FCSTD DOCUMENT  (FreeCAD 0.21R33771 (Git))
Label: Noise_Toaster_Classic
License: All rights reserved
LicenseURL: http://en.wikipedia.org/wiki/All_rights_reserved
objects: App::Link×10, App::DocumentObjectGroup×3, PartDesign::CoordinateSystem×1, App::FeaturePython×1, App::Part×1, Spreadsheet::Sheet×1, Image::ImagePlane×1
note: 1 computed .brp shape members not serialized (recipe doc carries the construction recipe); baked Part::Feature solids carry a one-line shape summary decoded from their .brp
EXTERNAL_REF file=Front_Panel.FCStd obj=Body
EXTERNAL_REF file=Side_Panel-B.FCStd obj=SP_B_LCS
EXTERNAL_REF file=Side_Panel-B.FCStd obj=Body
EXTERNAL_REF file=Side_Panel-A.FCStd obj=Body
EXTERNAL_REF file=Back_Panel.FCStd obj=Body

FEATURE [PartDesign::CoordinateSystem] LCS_Origin
  AttacherType = Attacher::AttachEngine3D
  MapMode = 2
  Support = -> [X_Axis]
FEATURE [App::DocumentObjectGroup] Constraints
FEATURE [App::FeaturePython] Variables  # WARN: FeaturePython — macro-defined, semantics opaque (R4)
  Type = App::PropertyContainer
FEATURE [App::DocumentObjectGroup] Configurations
FEATURE [App::Link] Link  label="Link - Back_Panel"
FEATURE [App::Link] Link001  label="Link - Front_Panel"
FEATURE [App::Link] Link002  label="Link - Side_Panel-A"
FEATURE [App::Link] Link003  label="Link - Side_Panle-B"
FEATURE [App::DocumentObjectGroup] Parts
  Group = -> [Link,Link001,Link002,Link003]
FEATURE [App::Link] Front001  label="Frontpanel"
  LinkPlacement = pos=(0,0,77.5) rot=(0,0,1;0rad)
  LinkedObject = -> <external Front_Panel.FCStd>#Body
  Placement = pos=(0,0,77.5) rot=(0,0,1;0rad)
  expr: .Placement.Base.z = <<measurements>>.Side_A_height - Front_Panel#<<measurements>>.Front_thickness
FEATURE [App::Link] Top
  AttachedBy = #SP_B_LCS
  AttachedTo = Parent Assembly#LCS_Origin
  LinkedObject = -> <external Side_Panel-B.FCStd>#Body
  SolverId = Asm4EE
  expr: Placement = LCS_Origin.Placement * AttachmentOffset * Side_Panel_B#SP_B_LCS.Placement ^ -1
FEATURE [App::Link] Left
  AttachedBy = #SP_A_LCS
  AttachedTo = Parent Assembly#LCS_Origin
  LinkPlacement = pos=(-3,0,0) rot=(0,0,1;0rad)
  LinkedObject = -> <external Side_Panel-A.FCStd>#Body
  Placement = pos=(-3,0,0) rot=(0,0,1;0rad)
  SolverId = Asm4EE
  expr: .Placement.Base.x = -Front_Panel#<<measurements>>.Side_B_o_thickness
FEATURE [App::Link] Right
  AttachedBy = #SP_A_LCS
  AttachedTo = Parent Assembly#LCS_Origin
  LinkPlacement = pos=(-3,175.1,0) rot=(0,0,1;0rad)
  LinkedObject = -> <external Side_Panel-A.FCStd>#Body
  Placement = pos=(-3,175.1,0) rot=(0,0,1;0rad)
  SolverId = Asm4EE
  expr: .Placement.Base.x = -Front_Panel#<<measurements>>.Side_B_o_thickness
  expr: .Placement.Base.y = Front_Panel#<<measurements>>.Front_width + Front_Panel#<<measurements>>.Side_A_thickness
FEATURE [App::Link] Back
  AttachedBy = #BP_LCS
  AttachedTo = Parent Assembly#LCS_Origin
  LinkPlacement = pos=(-3,-10,0) rot=(0,0,1;0rad)
  LinkedObject = -> <external Back_Panel.FCStd>#Body
  Placement = pos=(-3,-10,0) rot=(0,0,1;0rad)
  SolverId = Asm4EE
  expr: .Placement.Base.x = -Front_Panel#<<measurements>>.Side_B_o_thickness
  expr: .Placement.Base.y = -Front_Panel#<<measurements>>.Side_A_thickness
FEATURE [App::Link] Bottom
  AttachedBy = #SP_B_LCS
  AttachedTo = Parent Assembly#LCS_Origin
  AttachmentOffset = pos=(0,0,0) rot=(0,0,1;3.14159rad)
  LinkPlacement = pos=(165.1,165.1,0) rot=(0,0,1;3.14159rad)
  LinkedObject = -> <external Side_Panel-B.FCStd>#Body
  Placement = pos=(165.1,165.1,0) rot=(0,0,1;3.14159rad)
  SolverId = Asm4EE
  expr: .Placement.Base.x = Front_Panel#<<measurements>>.Front_height
  expr: .Placement.Base.y = Front_Panel#<<measurements>>.Front_width
FEATURE [App::Part] Assembly
  AssemblyType = Part::Link
  Group = -> [LCS_Origin,Constraints,Variables,Configurations,Front001,Top,Left,Right,Back,Bottom]
  Origin = -> Origin
  Type = Assembly
FEATURE [Spreadsheet::Sheet] Spreadsheet  label="measurements"
  cells = B2='Front Panel; B3='material; D3(Front_material)='Alu, Melal; B4='material thickness*; D4(Front_thickness)==2.5 mm; B5='measurements; B6='width*; D6(Front_width)==165.1 mm; B7='height; D7(Front_height)==Front_width; B9='Side Panel A; B10='material; D10(Side_A_material)='Wood, MDF; B11='material thickness*; D11(Side_A_thickness)==10 mm; B12='measurements; B13='width; D13(Side_A_width)==Front_height + 2 * Side_B_o_thickness; B14='height*; D14(Side_A_height)==80 mm; B16='Side Panlel B; B17='inner; B18='material; D18(Side_B_i_material)='Wood, MDF; B19='material thickness*; D19(Side_B_i_thickness)==10 mm; B20='measurements; B21='width; D21(Side_B_i_width)==Front_width; B22='height; D22(Side_B_i_height)==Side_B_o_height - Side_B_o_thickness; B23='outer; B24='material; D24(Side_B_o_material)='Wood, MDF; B25='material thickness*; D25(Side_B_o_thickness)==3 mm; B26='measurements; B27='width; D27(Side_B_o_width)==Front_width; B28='height; D28(Side_B_o_height)==Side_A_height; B30='Back Panel; B31='material; D31(Back_material)='Wood, MDF; B32='material thickness*; D32(Back_thickness)==3 mm; B33='measurements; B34='width; D34(Back_width)==Front_width + 2 * Side_A_thickness; B35='height; D35(Back_height)==Side_A_width; B37='* = reference measure
FEATURE [Image::ImagePlane] front_panel_classic_design  label="front panel classic design"
  Placement = pos=(82.55,82.55,80) rot=(0,0,1;1.5708rad)
  XSize = 257.211
  YSize = 194.496
  expr: .Placement.Base.x = <<measurements>>.Front_width / 2
  expr: .Placement.Base.y = <<measurements>>.Front_height / 2
  expr: .Placement.Base.z = <<measurements>>.Side_A_height

RESOLVED EXTERNAL PARTS (link-assembly join: the EXTERNAL_REF files above that resolve inside this repo's crawl, each included once):
---- part Back_Panel.FCStd = doc fcstd_5dd3100f07a6 ----
FCSTD DOCUMENT  (FreeCAD 0.21R33771 (Git))
Label: Back_Panel
License: All rights reserved
LicenseURL: http://en.wikipedia.org/wiki/All_rights_reserved
objects: Sketcher::SketchObject×1, PartDesign::Pad×1, PartDesign::CoordinateSystem×1, PartDesign::Body×1
note: 5 computed .brp shape members not serialized (recipe doc carries the construction recipe); baked Part::Feature solids carry a one-line shape summary decoded from their .brp
EXTERNAL_REF file=Noise_Toaster_Classic.FCStd obj=Spreadsheet

FEATURE [Sketcher::SketchObject] Sketch
  FullyConstrained = true
  MapMode = 5
  Support = -> [XY_Plane]
  expr: Constraints[10] = Noise_Toaster_Classic#<<measurements>>.Back_width
  expr: Constraints[9] = Noise_Toaster_Classic#<<measurements>>.Back_height
  sketch-geometry (61):
    g0: LineSegment StartX=0 StartY=0 StartZ=0 EndX=171.1 EndY=0 EndZ=0
    g1: LineSegment StartX=171.1 StartY=0 StartZ=0 EndX=171.1 EndY=185.1 EndZ=0
    g2: LineSegment StartX=171.1 StartY=185.1 StartZ=0 EndX=0 EndY=185.1 EndZ=0
    g3: LineSegment StartX=0 StartY=185.1 StartZ=0 EndX=0 EndY=0 EndZ=0
    g4: Circle CenterX=48.5 CenterY=48.5 CenterZ=0 NormalX=0 NormalY=0 NormalZ=1 AngleXU=0 Radius=2.5
    g5: Circle CenterX=48.5 CenterY=54.5 CenterZ=0 NormalX=0 NormalY=0 NormalZ=1 AngleXU=0 Radius=2.5
    g6: Circle CenterX=48.5 CenterY=60.5 CenterZ=0 NormalX=0 NormalY=0 NormalZ=1 AngleXU=0 Radius=2.5
    g7: Circle CenterX=48.5 CenterY=66.5 CenterZ=0 NormalX=0 NormalY=0 NormalZ=1 AngleXU=0 Radius=2.5
    g8: Circle CenterX=48.5 CenterY=72.5 CenterZ=0 NormalX=0 NormalY=0 NormalZ=1 AngleXU=0 Radius=2.5
    g9: Circle CenterX=48.5 CenterY=42.5 CenterZ=0 NormalX=0 NormalY=0 NormalZ=1 AngleXU=0 Radius=2.5
    g10: Circle CenterX=48.5 CenterY=36.5 CenterZ=0 NormalX=0 NormalY=0 NormalZ=1 AngleXU=0 Radius=2.5
    g11: Circle CenterX=48.5 CenterY=30.5 CenterZ=0 NormalX=0 NormalY=0 NormalZ=1 AngleXU=0 Radius=2.5
    g12: Circle CenterX=48.5 CenterY=24.5 CenterZ=0 NormalX=0 NormalY=0 NormalZ=1 AngleXU=0 Radius=2.5
    g13: Circle CenterX=36.5 CenterY=48.5 CenterZ=0 NormalX=0 NormalY=0 NormalZ=1 AngleXU=0 Radius=2.5
    g14: Circle CenterX=36.5 CenterY=54.5 CenterZ=0 NormalX=0 NormalY=0 NormalZ=1 AngleXU=0 Radius=2.5
    g15: Circle CenterX=36.5 CenterY=60.5 CenterZ=0 NormalX=0 NormalY=0 NormalZ=1 AngleXU=0 Radius=2.5
    g16: Circle CenterX=36.5 CenterY=66.5 CenterZ=0 NormalX=0 NormalY=0 NormalZ=1 AngleXU=0 Radius=2.5
    g17: Circle CenterX=36.5 CenterY=42.5 CenterZ=0 NormalX=0 NormalY=0 NormalZ=1 AngleXU=0 Radius=2.5
    g18: Circle CenterX=36.5 CenterY=36.5 CenterZ=0 NormalX=0 NormalY=0 NormalZ=1 AngleXU=0 Radius=2.5
    g19: Circle CenterX=36.5 CenterY=30.5 CenterZ=0 NormalX=0 NormalY=0 NormalZ=1 AngleXU=0 Radius=2.5
    g20: Circle CenterX=24.5 CenterY=48.5 CenterZ=0 NormalX=0 NormalY=0 NormalZ=1 AngleXU=0 Radius=2.5
    g21: Circle CenterX=24.5 CenterY=54.5 CenterZ=0 NormalX=0 NormalY=0 NormalZ=1 AngleXU=0 Radius=2.5
    g22: Circle CenterX=24.5 CenterY=42.5 CenterZ=0 NormalX=0 NormalY=0 NormalZ=1 AngleXU=0 Radius=2.5
    g23: Circle CenterX=42.5 CenterY=51.5 CenterZ=0 NormalX=0 NormalY=0 NormalZ=1 AngleXU=0 Radius=2.5
    g24: Circle CenterX=42.5 CenterY=45.5 CenterZ=0 NormalX=0 NormalY=0 NormalZ=1 AngleXU=0 Radius=2.5
    g25: Circle CenterX=42.5 CenterY=39.5 CenterZ=0 NormalX=0 NormalY=0 NormalZ=1 AngleXU=0 Radius=2.5
    g26: Circle CenterX=42.5 CenterY=33.5 CenterZ=0 NormalX=0 NormalY=0 NormalZ=1 AngleXU=0 Radius=2.5
    g27: Circle CenterX=42.5 CenterY=27.5 CenterZ=0 NormalX=0 NormalY=0 NormalZ=1 AngleXU=0 Radius=2.5
    g28: Circle CenterX=42.5 CenterY=57.5 CenterZ=0 NormalX=0 NormalY=0 NormalZ=1 AngleXU=0 Radius=2.5
    g29: Circle CenterX=42.5 CenterY=63.5 CenterZ=0 NormalX=0 NormalY=0 NormalZ=1 AngleXU=0 Radius=2.5
    g30: Circle CenterX=42.5 CenterY=69.5 CenterZ=0 NormalX=0 NormalY=0 NormalZ=1 AngleXU=0 Radius=2.5
    g31: Circle CenterX=30.5 CenterY=51.5 CenterZ=0 NormalX=0 NormalY=0 NormalZ=1 AngleXU=0 Radius=2.5
    g32: Circle CenterX=30.5 CenterY=57.5 CenterZ=0 NormalX=0 NormalY=0 NormalZ=1 AngleXU=0 Radius=2.5
    g33: Circle CenterX=30.5 CenterY=63.5 CenterZ=0 NormalX=0 NormalY=0 NormalZ=1 AngleXU=0 Radius=2.5
    g34: Circle CenterX=30.5 CenterY=45.5 CenterZ=0 NormalX=0 NormalY=0 NormalZ=1 AngleXU=0 Radius=2.5
    g35: Circle CenterX=30.5 CenterY=39.5 CenterZ=0 NormalX=0 NormalY=0 NormalZ=1 AngleXU=0 Radius=2.5
    g36: Circle CenterX=30.5 CenterY=33.5 CenterZ=0 NormalX=0 NormalY=0 NormalZ=1 AngleXU=0 Radius=2.5
    g37: Circle CenterX=54.5 CenterY=69.5 CenterZ=0 NormalX=0 NormalY=0 NormalZ=1 AngleXU=0 Radius=2.5
    g38: Circle CenterX=54.5 CenterY=63.5 CenterZ=0 NormalX=0 NormalY=0 NormalZ=1 AngleXU=0 Radius=2.5
    g39: Circle CenterX=54.5 CenterY=57.5 CenterZ=0 NormalX=0 NormalY=0 NormalZ=1 AngleXU=0 Radius=2.5
    g40: Circle CenterX=54.5 CenterY=51.5 CenterZ=0 NormalX=0 NormalY=0 NormalZ=1 AngleXU=0 Radius=2.5
    g41: Circle CenterX=54.5 CenterY=45.5 CenterZ=0 NormalX=0 NormalY=0 NormalZ=1 AngleXU=0 Radius=2.5
    g42: Circle CenterX=54.5 CenterY=39.5 CenterZ=0 NormalX=0 NormalY=0 NormalZ=1 AngleXU=0 Radius=2.5
    g43: Circle CenterX=54.5 CenterY=33.5 CenterZ=0 NormalX=0 NormalY=0 NormalZ=1 AngleXU=0 Radius=2.5
    g44: Circle CenterX=54.5 CenterY=27.5 CenterZ=0 NormalX=0 NormalY=0 NormalZ=1 AngleXU=0 Radius=2.5
    g45: Circle CenterX=60.5 CenterY=66.5 CenterZ=0 NormalX=0 NormalY=0 NormalZ=1 AngleXU=0 Radius=2.5
    g46: Circle CenterX=60.5 CenterY=60.5 CenterZ=0 NormalX=0 NormalY=0 NormalZ=1 AngleXU=0 Radius=2.5
    g47: Circle CenterX=60.5 CenterY=54.5 CenterZ=0 NormalX=0 NormalY=0 NormalZ=1 AngleXU=0 Radius=2.5
    g48: Circle CenterX=60.5 CenterY=48.5 CenterZ=0 NormalX=0 NormalY=0 NormalZ=1 AngleXU=0 Radius=2.5
    g49: Circle CenterX=60.5 CenterY=42.5 CenterZ=0 NormalX=0 NormalY=0 NormalZ=1 AngleXU=0 Radius=2.5
    g50: Circle CenterX=60.5 CenterY=36.5 CenterZ=0 NormalX=0 NormalY=0 NormalZ=1 AngleXU=0 Radius=2.5
    g51: Circle CenterX=60.5 CenterY=30.5 CenterZ=0 NormalX=0 NormalY=0 NormalZ=1 AngleXU=0 Radius=2.5
    g52: Circle CenterX=66.5 CenterY=63.5 CenterZ=0 NormalX=0 NormalY=0 NormalZ=1 AngleXU=0 Radius=2.5
    g53: Circle CenterX=66.5 CenterY=57.5 CenterZ=0 NormalX=0 NormalY=0 NormalZ=1 AngleXU=0 Radius=2.5
    g54: Circle CenterX=66.5 CenterY=51.5 CenterZ=0 NormalX=0 NormalY=0 NormalZ=1 AngleXU=0 Radius=2.5
    g55: Circle CenterX=66.5 CenterY=45.5 CenterZ=0 NormalX=0 NormalY=0 NormalZ=1 AngleXU=0 Radius=2.5
    g56: Circle CenterX=66.5 CenterY=39.5 CenterZ=0 NormalX=0 NormalY=0 NormalZ=1 AngleXU=0 Radius=2.5
    g57: Circle CenterX=66.5 CenterY=33.5 CenterZ=0 NormalX=0 NormalY=0 NormalZ=1 AngleXU=0 Radius=2.5
    g58: Circle CenterX=72.5 CenterY=54.5 CenterZ=0 NormalX=0 NormalY=0 NormalZ=1 AngleXU=0 Radius=2.5
    g59: Circle CenterX=72.5 CenterY=48.5 CenterZ=0 NormalX=0 NormalY=0 NormalZ=1 AngleXU=0 Radius=2.5
    g60: Circle CenterX=72.5 CenterY=42.5 CenterZ=0 NormalX=0 NormalY=0 NormalZ=1 AngleXU=0 Radius=2.5
  constraints (182):
    c: Coincident(g0,g1)
    c: Coincident(g1,g2)
    c: Coincident(g2,g3)
    c: Coincident(g3,g0)
    c: Horizontal(g0)
    c: Horizontal(g2)
    c: Vertical(g1)
    c: Vertical(g3)
    c: Coincident(g0,g-1)
    c: DistanceX(g2,g2) = 171.1
    c: DistanceY(g3,g3) = 185.1
    c: Radius(g4) = 2.5
    c: Vertical(g7,g6)
    c: Vertical(g6,g5)
    c: Equal(g4,g5)
    c: Equal(g5,g6)
    c: Equal(g6,g7)
    c: Vertical(g8,g7)
    c: Equal(g8,g7)
    c: Distance(g6,g5) = 6
    c: Distance(g7,g6) = 6
    c: Distance(g8,g7) = 6
    c: Equal(g9,g10)
    c: Equal(g10,g11)
    c: Equal(g11,g12)
    c: Equal(g4,g9)
    c: Vertical(g9,g10)
    c: Vertical(g10,g11)
    c: Vertical(g11,g12)
    c: Distance(g9,g10) = 6
    c: Distance(g10,g11) = 6
    c: Distance(g11,g12) = 6
    c: Vertical(g13,g14)
    c: Vertical(g14,g15)
    c: Vertical(g15,g16)
    c: Radius(g13) = 2.5
    c: Equal(g13,g14)
    c: Equal(g14,g15)
    c: Equal(g15,g16)
    c: Equal(g13,g17)
    c: Equal(g17,g18)
    c: Equal(g18,g19)
    c: Vertical(g13,g17)
    c: Vertical(g17,g18)
    c: Vertical(g18,g19)
    c: Distance(g16,g15) = 6
    c: Distance(g15,g14) = 6
    c: Distance(g13,g14) = 6
    c: Distance(g13,g17) = 6
    c: Distance(g18,g17) = 6
    c: Distance(g19,g18) = 6
    c: Vertical(g22,g20)
    c: Vertical(g20,g21)
    c: Distance(g13,g20) = 12
    c: Radius(g20) = 2.5
    c: Equal(g20,g21)
    c: Distance(g20,g21) = 6
    c: Distance(g20,g22) = 6
    c: Horizontal(g13,g20)
    c: Equal(g20,g22)
    c: Vertical(g34,g35)
    c: Vertical(g35,g36)
    c: Vertical(g36,g31)
    c: Vertical(g31,g32)
    c: Vertical(g32,g33)
    c: Vertical(g26,g27)
    c: Vertical(g27,g25)
    c: Vertical(g25,g24)
    c: Vertical(g24,g23)
    c: Vertical(g23,g28)
    c: Vertical(g28,g29)
    c: Vertical(g29,g30)
    c: Equal(g4,g24)
    c: Equal(g24,g25)
    c: Equal(g25,g26)
    c: Equal(g26,g27)
    c: Equal(g27,g23)
    c: Equal(g23,g28)
    c: Equal(g28,g29)
    c: Equal(g29,g30)
    c: Equal(g30,g33)
    c: Equal(g33,g32)
    c: Equal(g32,g31)
    c: Equal(g31,g34)
    c: Equal(g34,g35)
    c: Equal(g35,g36)
    c: Distance(g30,g29) = 6
    c: Distance(g29,g28) = 6
    c: Distance(g28,g23) = 6
    c: Distance(g23,g24) = 6
    c: Distance(g24,g25) = 6
    c: Distance(g25,g26) = 6
    c: Distance(g26,g27) = 6
    c: Distance(g36,g35) = 6
    c: Distance(g34,g35) = 6
    c: Distance(g31,g34) = 6
    c: Distance(g32,g31) = 6
    c: Distance(g33,g32) = 6
    c: Distance(g23,g31) = 12
    c: Horizontal(g23,g31)
    c: Equal(g11,g43)
    c: Equal(g43,g42)
    c: Equal(g42,g41)
    c: Equal(g41,g40)
    c: Equal(g40,g39)
    c: Equal(g39,g38)
    c: Equal(g38,g37)
    c: Equal(g37,g44)
    c: Vertical(g37,g38)
    c: Vertical(g38,g39)
    c: Vertical(g39,g40)
    c: Vertical(g40,g41)
    c: Vertical(g41,g42)
    c: Vertical(g42,g43)
    c: Vertical(g43,g44)
    c: Horizontal(g37,g30)
    c: DistanceX(g30,g37) = 12
    c: Distance(g37,g38) = 6
    c: Distance(g38,g39) = 6
    c: Distance(g39,g40) = 6
    c: Distance(g40,g41) = 6
    c: Distance(g41,g42) = 6
    c: Distance(g42,g43) = 6
    c: Distance(g43,g44) = 6
    c: Vertical(g45,g46)
    c: Vertical(g46,g47)
    c: Vertical(g47,g48)
    c: Vertical(g48,g49)
    c: Vertical(g49,g50)
    c: Vertical(g50,g51)
    c: Equal(g45,g46)
    c: Equal(g46,g47)
    c: Equal(g47,g48)
    c: Equal(g48,g49)
    c: Equal(g49,g50)
    c: Equal(g50,g51)
    c: Equal(g51,g37)
    c: Horizontal(g45,g7)
    c: Distance(g45,g46) = 6
    c: Distance(g46,g47) = 6
    c: Distance(g47,g48) = 6
    c: Distance(g48,g49) = 6
    c: Distance(g49,g50) = 6
    c: Distance(g50,g51) = 6
    c: Vertical(g52,g53)
    c: Vertical(g53,g54)
    c: Vertical(g54,g55)
    c: Vertical(g55,g56)
    c: Vertical(g56,g57)
    c: Equal(g52,g53)
    c: Equal(g53,g54)
    c: Equal(g54,g55)
    c: Equal(g55,g56)
    c: Equal(g56,g57)
    c: Equal(g57,g45)
    c: DistanceY(g53,g52) = 6
    c: DistanceY(g54,g53) = 6
    c: DistanceY(g55,g54) = 6
    c: DistanceY(g56,g55) = 6
    c: DistanceX(g43,g57) = 12
    c: Horizontal(g57,g43)
    c: Distance(g57,g56) = 6
    c: Equal(g58,g59)
    c: Equal(g59,g60)
    c: Equal(g60,g53)
    c: Vertical(g58,g59)
    c: Vertical(g59,g60)
    c: Horizontal(g59,g48)
    c: DistanceY(g59,g58) = 6
    c: DistanceY(g60,g59) = 6
    c: DistanceX(g48,g59) = 12
    c: Distance(g4,g0) = 48.5
    c: Distance(g4,g3) = 48.5
    c: DistanceX(g4,g40) = 6
    c: DistanceX(g14,g5) = 12
    c: DistanceY(g24,g4) = 3
    c: Vertical(g9,g4)
    c: DistanceY(g9,g4) = 6
    c: DistanceY(g4,g5) = 6
    c: Vertical(g5,g4)
    c: DistanceX(g5,g47) = 12
    c: Horizontal(g5,g14)
FEATURE [PartDesign::Pad] Pad
  Direction = (0,0,1)
  Length = 3
  Length2 = 10
  Profile = -> Sketch
  ReferenceAxis = -> Sketch [N_Axis]
  Reversed = true
  Type = 0
  expr: Length = Noise_Toaster_Classic#<<measurements>>.Back_thickness
FEATURE [PartDesign::CoordinateSystem] BP_LCS
  AttacherType = Attacher::AttachEngine3D
  Support = -> [Pad]
FEATURE [PartDesign::Body] Body  label="Körper"
  Group = -> [Sketch,Pad,BP_LCS]
  Origin = -> Origin
  Tip = -> Pad
---- part Front_Panel.FCStd = doc fcstd_5506be05636f ----
FCSTD DOCUMENT  (FreeCAD 0.21R33771 (Git))
Label: Front_Panel
License: All rights reserved
LicenseURL: http://en.wikipedia.org/wiki/All_rights_reserved
objects: Sketcher::SketchObject×1, PartDesign::Pad×1, PartDesign::CoordinateSystem×1, PartDesign::Body×1
note: 5 computed .brp shape members not serialized (recipe doc carries the construction recipe); baked Part::Feature solids carry a one-line shape summary decoded from their .brp
EXTERNAL_REF file=Noise_Toaster_Classic.FCStd obj=Spreadsheet

FEATURE [Sketcher::SketchObject] Sketch  label="dimensions"
  FullyConstrained = true
  Support = -> [XY_Plane]
  expr: Constraints[9] = Noise_Toaster_Classic#<<measurements>>.Front_width
  sketch-geometry (33):
    g0: LineSegment StartX=0 StartY=0 StartZ=0 EndX=165.1 EndY=0 EndZ=0
    g1: LineSegment StartX=165.1 StartY=0 StartZ=0 EndX=165.1 EndY=165.1 EndZ=0
    g2: LineSegment StartX=165.1 StartY=165.1 StartZ=0 EndX=0 EndY=165.1 EndZ=0
    g3: LineSegment StartX=0 StartY=165.1 StartZ=0 EndX=0 EndY=0 EndZ=0
    g4: Circle CenterX=5 CenterY=157.6 CenterZ=0 NormalX=0 NormalY=0 NormalZ=1 AngleXU=0 Radius=2
    g5: Circle CenterX=5 CenterY=7.5 CenterZ=0 NormalX=0 NormalY=0 NormalZ=1 AngleXU=0 Radius=2
    g6: Circle CenterX=160.1 CenterY=7.5 CenterZ=0 NormalX=0 NormalY=0 NormalZ=1 AngleXU=0 Radius=2
    g7: Circle CenterX=160.1 CenterY=157.6 CenterZ=0 NormalX=0 NormalY=0 NormalZ=1 AngleXU=0 Radius=2
    g8: Circle CenterX=34.5 CenterY=26.5 CenterZ=0 NormalX=0 NormalY=0 NormalZ=1 AngleXU=0 Radius=5.5
    g9: Circle CenterX=34.5 CenterY=46.7 CenterZ=0 NormalX=0 NormalY=0 NormalZ=1 AngleXU=0 Radius=3
    g10: Circle CenterX=34.5 CenterY=66.9 CenterZ=0 NormalX=0 NormalY=0 NormalZ=1 AngleXU=0 Radius=5.5
    g11: Circle CenterX=34.5 CenterY=93.9 CenterZ=0 NormalX=0 NormalY=0 NormalZ=1 AngleXU=0 Radius=5.5
    g12: Circle CenterX=34.5 CenterY=115.2 CenterZ=0 NormalX=0 NormalY=0 NormalZ=1 AngleXU=0 Radius=3
    g13: Circle CenterX=18.8 CenterY=117.9 CenterZ=0 NormalX=0 NormalY=0 NormalZ=1 AngleXU=0 Radius=2
    g14: Circle CenterX=25.35 CenterY=138.2 CenterZ=0 NormalX=0 NormalY=0 NormalZ=1 AngleXU=0 Radius=4.5
    g15: Circle CenterX=57.35 CenterY=138.2 CenterZ=0 NormalX=0 NormalY=0 NormalZ=1 AngleXU=0 Radius=5.5
    g16: Circle CenterX=98.9481 CenterY=138.6 CenterZ=0 NormalX=0 NormalY=0 NormalZ=1 AngleXU=0 Radius=3
    g17: Circle CenterX=138.046 CenterY=138.2 CenterZ=0 NormalX=0 NormalY=0 NormalZ=1 AngleXU=0 Radius=3
    g18: Circle CenterX=66 CenterY=21.7 CenterZ=0 NormalX=0 NormalY=0 NormalZ=1 AngleXU=0 Radius=3
    g19: Circle CenterX=83.3 CenterY=21.7 CenterZ=0 NormalX=0 NormalY=0 NormalZ=1 AngleXU=0 Radius=3
    g20: Circle CenterX=74.1 CenterY=54.4 CenterZ=0 NormalX=0 NormalY=0 NormalZ=1 AngleXU=0 Radius=5.5
    g21: Circle CenterX=74.1 CenterY=81.3 CenterZ=0 NormalX=0 NormalY=0 NormalZ=1 AngleXU=0 Radius=5.5
    g22: Circle CenterX=74.1 CenterY=108.2 CenterZ=0 NormalX=0 NormalY=0 NormalZ=1 AngleXU=0 Radius=5.5
    g23: Circle CenterX=98.9481 CenterY=108.2 CenterZ=0 NormalX=0 NormalY=0 NormalZ=1 AngleXU=0 Radius=3
    g24: Circle CenterX=116.3 CenterY=26.4 CenterZ=0 NormalX=0 NormalY=0 NormalZ=1 AngleXU=0 Radius=5.5
    g25: Circle CenterX=116.3 CenterY=56.4 CenterZ=0 NormalX=0 NormalY=0 NormalZ=1 AngleXU=0 Radius=5.5
    g26: Circle CenterX=143.2 CenterY=22.8 CenterZ=0 NormalX=0 NormalY=0 NormalZ=1 AngleXU=0 Radius=3.5
    g27: Circle CenterX=143.7 CenterY=42.5937 CenterZ=0 NormalX=0 NormalY=0 NormalZ=1 AngleXU=0 Radius=3
    g28: Circle CenterX=143.7 CenterY=56.2937 CenterZ=0 NormalX=0 NormalY=0 NormalZ=1 AngleXU=0 Radius=2
    g29: Circle CenterX=139.1 CenterY=85.8 CenterZ=0 NormalX=0 NormalY=0 NormalZ=1 AngleXU=0 Radius=3
    g30: Circle CenterX=138.7 CenterY=108.096 CenterZ=0 NormalX=0 NormalY=0 NormalZ=1 AngleXU=0 Radius=5.5
    g31: Circle CenterX=112.7 CenterY=85.8 CenterZ=0 NormalX=0 NormalY=0 NormalZ=1 AngleXU=0 Radius=3
    g32: Circle CenterX=117.3 CenterY=118.4 CenterZ=0 NormalX=0 NormalY=0 NormalZ=1 AngleXU=0 Radius=2.5
  constraints (98):
    c: Coincident(g0,g1)
    c: Coincident(g1,g2)
    c: Coincident(g2,g3)
    c: Coincident(g3,g0)
    c: Horizontal(g0)
    c: Horizontal(g2)
    c: Vertical(g1)
    c: Vertical(g3)
    c: Coincident(g0,g-1)
    c: DistanceX(g0,g0) = 165.1
    c: Equal(g0,g3)
    c: Distance(g4,g2) = 7.5
    c: Distance(g4,g3) = 5
    c: Radius(g4) = 2
    c: Equal(g4,g7)
    c: Equal(g5,g6)
    c: Equal(g4,g5)
    c: Distance(g7,g1) = 5
    c: Distance(g7,g2) = 7.5
    c: Distance(g5,g3) = 5
    c: Distance(g5,g0) = 7.5
    c: Distance(g6,g1) = 5
    c: Distance(g6,g0) = 7.5
    c: Distance(g8,g0) = 26.5
    c: Distance(g8,g3) = 34.5
    c: Radius(g8) = 5.5
    c: Distance(g8,g9) = 20.2
    c: Vertical(g9,g8)
    c: Radius(g9) = 3
    c: Distance(g9,g10) = 20.2
    c: Vertical(g10,g9)
    c: Radius(g10) = 5.5
    c: Vertical(g11,g10)
    c: Distance(g11,g10) = 27
    c: Radius(g11) = 5.5
    c: Vertical(g12,g11)
    c: Radius(g12) = 3
    c: Distance(g12,g11) = 21.3
    c: Distance(g13,g2) = 47.2
    c: Distance(g13,g3) = 18.8
    c: Radius(g13) = 2
    c: Distance(g14,g2) = 26.9
    c: Radius(g14) = 4.5
    c: Distance(g14,g3) = 25.35
    c: Horizontal(g15,g14)
    c: Horizontal(g17,g15)
    c: Radius(g16) = 3
    c: Radius(g17) = 3
    c: Radius(g15) = 5.5
    c: Distance(g14,g15) = 32
    c: Distance(g16,g15) = 41.6
    c: Distance(g16,g17) = 39.1
    c: Distance(g16,g2) = 23.5
    c: Radius(g18) = 3
    c: Radius(g19) = 3
    c: Horizontal(g19,g18)
    c: Distance(g18,g19) = 17.3
    c: DistanceY(g0,g18) = 21.7
    c: Distance(g18,g3) = 66
    c: Radius(g20) = 5.5
    c: Radius(g21) = 5.5
    c: Radius(g22) = 5.5
    c: Vertical(g22,g21)
    c: Vertical(g21,g20)
    c: Distance(g20,g3) = 74.1
    c: Distance(g20,g21) = 26.9
    c: Distance(g21,g22) = 26.9
    c: Distance(g20,g0) = 54.4
    c: Radius(g23) = 3
    c: Vertical(g16,g23)
    c: Horizontal(g23,g22)
    c: Vertical(g24,g25)
    c: Distance(g24,g0) = 26.4
    c: Distance(g24,g25) = 30
    c: Radius(g24) = 5.5
    c: Radius(g25) = 5.5
    c: Distance(g26,g1) = 21.9
    c: Distance(g27,g1) = 21.4
    c: Vertical(g27,g28)
    c: Distance(g28,g27) = 13.7
    c: Radius(g28) = 2
    c: Radius(g27) = 3
    c: Distance(g27,g26) = 19.8
    c: Distance(g26,g0) = 22.8
    c: Radius(g26) = 3.5
    c: Distance(g24,g1) = 48.8
    c: Distance(g29,g1) = 26
    c: Distance(g30,g1) = 26.4
    c: Distance(g30,g29) = 22.3
    c: Radius(g30) = 5.5
    c: Radius(g29) = 3
    c: Distance(g29,g0) = 85.8
    c: Horizontal(g29,g31)
    c: Radius(g31) = 3
    c: Distance(g29,g31) = 26.4
    c: Distance(g32,g1) = 47.8
    c: Radius(g32) = 2.5
    c: Distance(g32,g2) = 46.7
FEATURE [PartDesign::Pad] Pad
  Direction = (0,0,1)
  Length = 2.5
  Length2 = 10
  Profile = -> Sketch
  ReferenceAxis = -> Sketch [N_Axis]
  Type = 0
  expr: Length = Noise_Toaster_Classic#<<measurements>>.Front_thickness
FEATURE [PartDesign::CoordinateSystem] Front_LCS001  label="Front_LCS"
  AttacherType = Attacher::AttachEngine3D
  Support = -> [Pad,Origin]
FEATURE [PartDesign::Body] Body  label="Körper"
  Group = -> [Sketch,Pad,Front_LCS001]
  Origin = -> Origin
  Tip = -> Pad
---- part Side_Panel-A.FCStd = doc fcstd_a0021b3aa503 ----
FCSTD DOCUMENT  (FreeCAD 0.21R33771 (Git))
Label: Side_Panel-A
License: All rights reserved
LicenseURL: http://en.wikipedia.org/wiki/All_rights_reserved
objects: Sketcher::SketchObject×1, PartDesign::Pad×1, PartDesign::CoordinateSystem×1, PartDesign::Body×1
note: 5 computed .brp shape members not serialized (recipe doc carries the construction recipe); baked Part::Feature solids carry a one-line shape summary decoded from their .brp
EXTERNAL_REF file=Noise_Toaster_Classic.FCStd obj=Spreadsheet

FEATURE [Sketcher::SketchObject] Sketch
  FullyConstrained = true
  MapMode = 5
  Placement = pos=(0,0,0) rot=(1,0,0;1.5708rad)
  Support = -> [XZ_Plane]
  expr: Constraints[10] = Noise_Toaster_Classic#<<measurements>>.Side_A_height
  expr: Constraints[9] = Noise_Toaster_Classic#<<measurements>>.Side_A_width
  sketch-geometry (4):
    g0: LineSegment StartX=0 StartY=0 StartZ=0 EndX=171.1 EndY=0 EndZ=0
    g1: LineSegment StartX=171.1 StartY=0 StartZ=0 EndX=171.1 EndY=80 EndZ=0
    g2: LineSegment StartX=171.1 StartY=80 StartZ=0 EndX=0 EndY=80 EndZ=0
    g3: LineSegment StartX=0 StartY=80 StartZ=0 EndX=0 EndY=0 EndZ=0
  constraints (11):
    c: Coincident(g0,g1)
    c: Coincident(g1,g2)
    c: Coincident(g2,g3)
    c: Coincident(g3,g0)
    c: Horizontal(g0)
    c: Horizontal(g2)
    c: Vertical(g1)
    c: Vertical(g3)
    c: Coincident(g0,g-1)
    c: DistanceX(g2,g2) = 171.1
    c: DistanceY(g3,g3) = 80
FEATURE [PartDesign::Pad] Pad
  Direction = (0,-1,-2e-16)
  Length = 10
  Length2 = 10
  Placement = pos=(0,0,0) rot=(1,0,0;1.5708rad)
  Profile = -> Sketch
  ReferenceAxis = -> Sketch [N_Axis]
  Type = 0
  expr: Length = Noise_Toaster_Classic#<<measurements>>.Side_A_thickness
FEATURE [PartDesign::CoordinateSystem] SP_A_LCS
  AttacherType = Attacher::AttachEngine3D
  Support = -> [Pad]
FEATURE [PartDesign::Body] Body  label="Körper"
  Group = -> [Sketch,Pad,SP_A_LCS]
  Origin = -> Origin
  Tip = -> Pad
---- part Side_Panel-B.FCStd = doc fcstd_bd6a5a330df8 ----
FCSTD DOCUMENT  (FreeCAD 0.21R33771 (Git))
Label: Side_Panel-B
License: All rights reserved
LicenseURL: http://en.wikipedia.org/wiki/All_rights_reserved
objects: Sketcher::SketchObject×2, PartDesign::Pad×2, PartDesign::CoordinateSystem×1, PartDesign::Body×1
note: 8 computed .brp shape members not serialized (recipe doc carries the construction recipe); baked Part::Feature solids carry a one-line shape summary decoded from their .brp
EXTERNAL_REF file=Noise_Toaster_Classic.FCStd obj=Spreadsheet

FEATURE [Sketcher::SketchObject] Sketch  label="outer"
  FullyConstrained = true
  MapMode = 5
  Placement = pos=(0,0,0) rot=(0.57735,0.57735,0.57735;2.0944rad)
  Support = -> [YZ_Plane]
  expr: Constraints[10] = Noise_Toaster_Classic#<<measurements>>.Side_B_o_height
  expr: Constraints[9] = Noise_Toaster_Classic#<<measurements>>.Side_B_o_width
  sketch-geometry (4):
    g0: LineSegment StartX=0 StartY=0 StartZ=0 EndX=165.1 EndY=0 EndZ=0
    g1: LineSegment StartX=165.1 StartY=0 StartZ=0 EndX=165.1 EndY=80 EndZ=0
    g2: LineSegment StartX=165.1 StartY=80 StartZ=0 EndX=0 EndY=80 EndZ=0
    g3: LineSegment StartX=0 StartY=80 StartZ=0 EndX=0 EndY=0 EndZ=0
  constraints (11):
    c: Coincident(g0,g1)
    c: Coincident(g1,g2)
    c: Coincident(g2,g3)
    c: Coincident(g3,g0)
    c: Horizontal(g0)
    c: Horizontal(g2)
    c: Vertical(g1)
    c: Vertical(g3)
    c: Coincident(g0,g-1)
    c: DistanceX(g2,g2) = 165.1
    c: DistanceY(g3,g3) = 80
FEATURE [PartDesign::Pad] Pad
  Direction = (1,-2e-16,3e-16)
  Length = 3
  Length2 = 10
  Placement = pos=(0,0,0) rot=(1,1,1;2.0944rad)
  Profile = -> Sketch
  ReferenceAxis = -> Sketch [N_Axis]
  Reversed = true
  Type = 0
  expr: Length = Noise_Toaster_Classic#<<measurements>>.Side_B_o_thickness
FEATURE [Sketcher::SketchObject] Sketch001  label="innter"
  FullyConstrained = true
  MapMode = 5
  Placement = pos=(0,0,0) rot=(0.57735,0.57735,0.57735;2.0944rad)
  Support = -> [YZ_Plane]
  expr: Constraints[10] = Noise_Toaster_Classic#<<measurements>>.Side_B_i_height
  expr: Constraints[9] = Noise_Toaster_Classic#<<measurements>>.Side_B_i_width
  sketch-geometry (4):
    g0: LineSegment StartX=0 StartY=0 StartZ=0 EndX=165.1 EndY=0 EndZ=0
    g1: LineSegment StartX=165.1 StartY=0 StartZ=0 EndX=165.1 EndY=77 EndZ=0
    g2: LineSegment StartX=165.1 StartY=77 StartZ=0 EndX=0 EndY=77 EndZ=0
    g3: LineSegment StartX=0 StartY=77 StartZ=0 EndX=0 EndY=0 EndZ=0
  constraints (11):
    c: Coincident(g0,g1)
    c: Coincident(g1,g2)
    c: Coincident(g2,g3)
    c: Coincident(g3,g0)
    c: Horizontal(g0)
    c: Horizontal(g2)
    c: Vertical(g1)
    c: Vertical(g3)
    c: Coincident(g0,g-1)
    c: DistanceX(g2,g2) = 165.1
    c: DistanceY(g3,g3) = 77
FEATURE [PartDesign::Pad] Pad001
  BaseFeature = -> Pad
  Direction = (1,-2e-16,3e-16)
  Length = 10
  Length2 = 10
  Placement = pos=(0,0,0) rot=(1,1,1;2.0944rad)
  Profile = -> Sketch001
  ReferenceAxis = -> Sketch001 [N_Axis]
  Type = 0
  expr: Length = Noise_Toaster_Classic#<<measurements>>.Side_B_i_thickness
FEATURE [PartDesign::CoordinateSystem] SP_B_LCS
  AttacherType = Attacher::AttachEngine3D
  Support = -> [Pad001,Pad]
FEATURE [PartDesign::Body] Body  label="Körper"
  Group = -> [Sketch,Pad,Sketch001,Pad001,SP_B_LCS]
  Origin = -> Origin
  Tip = -> Pad001
